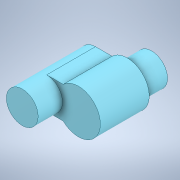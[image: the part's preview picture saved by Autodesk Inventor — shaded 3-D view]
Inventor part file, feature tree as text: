
AUTODESK INVENTOR PART (.ipt)
format: ipt  version: 2022 (Build 260153000, 153)  size: 137,728 bytes
history: native  units: in
note: dims shown in document units (in); Inventor stores cm internally (conversion verified against a paired STEP export)
features: extrude x3, sketch x2, projected_geometry x1
ambient origin geometry x8: Origin, YZ Plane, XZ Plane, XY Plane, X Axis, Y Axis, Z Axis, Center Point
bodies: Solid1 (feature_tree)
feature tree (6):
  sketch  "Sketch2"  dims[d0=0.3937in d1=0.0in d2=0.1969in d3=0.0in]
  extrude  "Extrusion1"  Depth=0.1969in TaperAngle=0.0deg
  extrude  "Extrusion2"  Depth=0.2559in
  extrude  "Extrusion3"  Depth=0.2559in
  sketch  "Sketch3"  dims[d4=0.1969in d5=0.0in d6=0.2559in d7=0.3543in d8=0.2559in d9=0.2559in]
  projected_geometry  "Projected Loop3"
